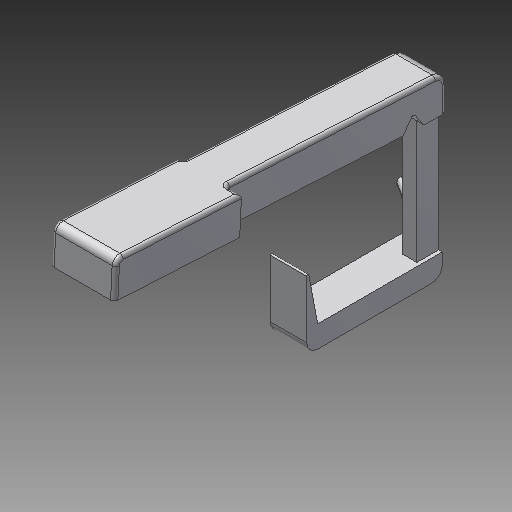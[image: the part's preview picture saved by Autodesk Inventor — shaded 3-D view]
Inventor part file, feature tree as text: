
AUTODESK INVENTOR PART (.ipt)
format: ipt  version: 2018 (Build 220112000, 112)  size: 308,736 bytes
history: native  units: mm
features: extrude x7, fillet x6, other x3, draft x1, chamfer x1
ambient origin geometry x8: Origin, YZ Plane, XZ Plane, XY Plane, X Axis, Y Axis, Z Axis, Center Point
bodies: Solid1 (feature_tree)
feature tree (18):
  other  "Key Sketch"
  extrude  "Upper Key"  Depth=10.0mm
  extrude  "Lower Key"  Depth=1.0mm
  other  "Hinge Cut Sketch"
  extrude  "Hinge Cut"  Depth=10.0mm TaperAngle=0.0deg
  extrude  "Hinge Cut 2"  Depth=3.0mm
  other  "Lever Sketch"
  extrude  "Vertical Lever"  Depth=3.0mm
  extrude  "Horizontal Lever"  Depth=33.6625mm
  extrude  "Spring Hook"  Depth=0.5mm
  draft  "FaceDraft3"
  chamfer  "Chamfer1"  Distance=3.0mm
  fillet  "Fillet9"  Radius=6.0mm
  fillet  "Fillet10"  Radius=4.0mm
  fillet  "Fillet5"  Radius=10.0mm
  fillet  "Fillet4"  [1 undecoded]
  fillet  "Fillet11"  Radius=3.0mm
  fillet  "Fillet14"  Radius=2.3mm
note: 1 required parameter value undecoded (feature->parameter linkage not recoverable at this tier; creation-order binding heuristic only, values carry confidence <= 0.55)
